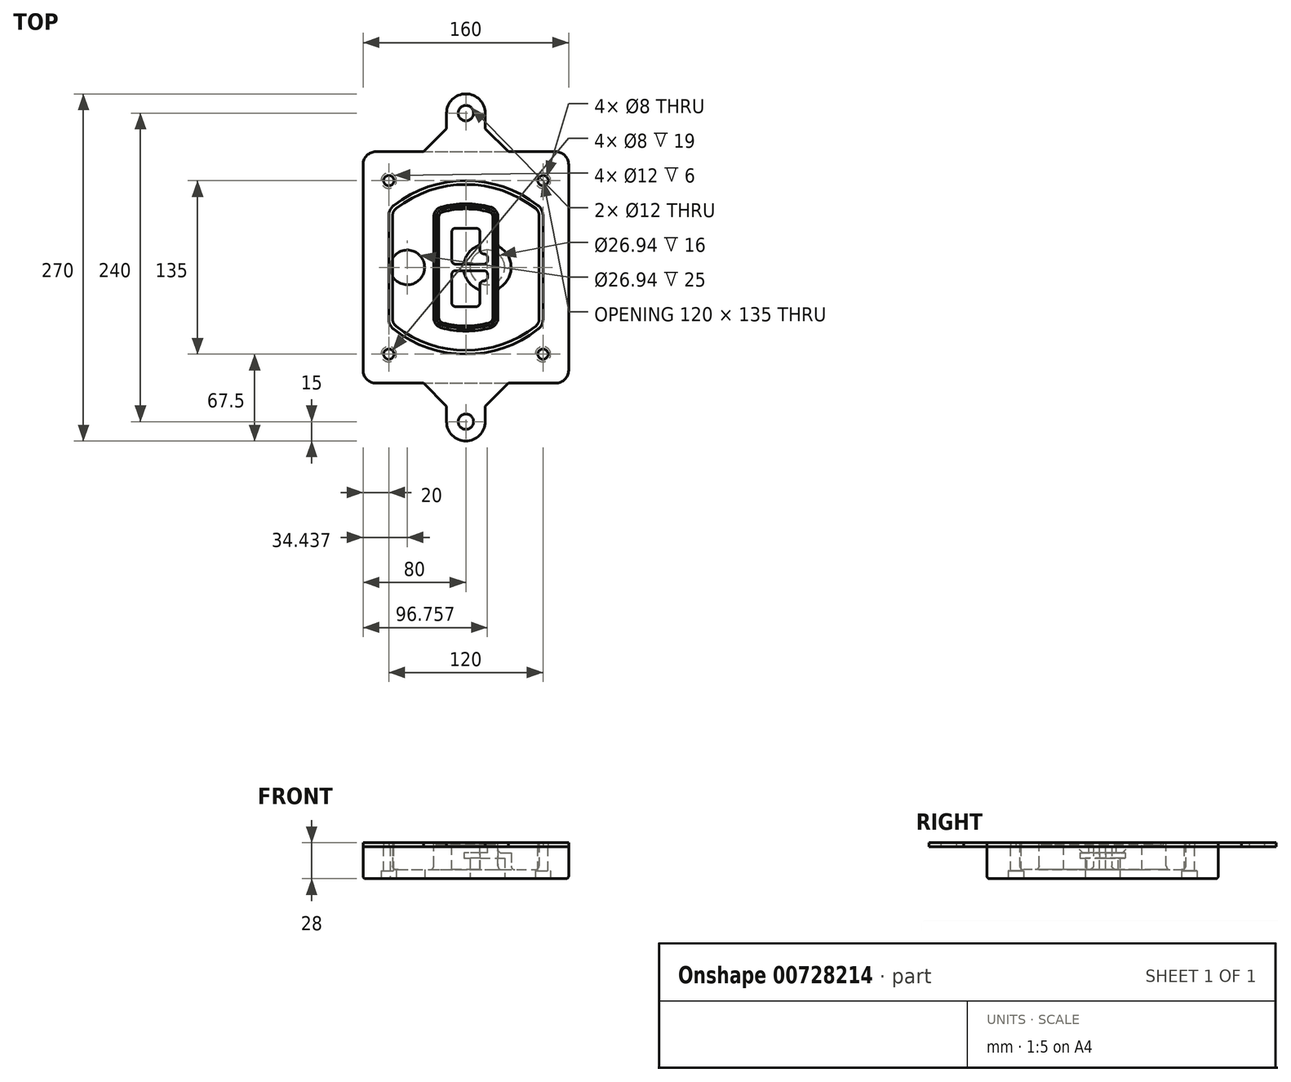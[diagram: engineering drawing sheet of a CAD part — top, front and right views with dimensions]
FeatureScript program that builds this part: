
annotation { "Feature Type Name" : "Feature", "Feature Type Description" : "" }
export const myFeature = defineFeature(function(context is Context, id is Id, definition is map)
    precondition{}
    {
        {
            var Q0;
            Q0=qCreatedBy(makeId("Top.planeOp"),FACE);
            var sketch = newSketch(context, id + "F0", { "sketchPlane" : qUnion([Q0])});
            skPoint(sketch, "E0.rect.middle", {"position": v(0, 0) * mm});
            skLineSegment(sketch, "E1.bottom", {"start": v(-70, -90) * mm, "end": v(70, -90) * mm});
            skLineSegment(sketch, "E1.top", {"start": v(-70, 90) * mm, "end": v(70, 90) * mm});
            skLineSegment(sketch, "E1.left", {"start": v(-80, -80) * mm, "end": v(-80, 80) * mm});
            skLineSegment(sketch, "E1.right", {"start": v(80, -80) * mm, "end": v(80, 80) * mm});
            skLineSegment(sketch, "E2", {"start": v(-80, 90) * mm, "end": v(80, -90) * mm, "construction": true});
            skLineSegment(sketch, "E3", {"start": v(80, 90) * mm, "end": v(-80, -90) * mm, "construction": true});
            skCircle(sketch, "E4", {"center": v(-60, 67.5) * mm, "radius": 4 * mm});
            skCircle(sketch, "E5", {"center": v(60, 67.5) * mm, "radius": 4 * mm});
            skCircle(sketch, "E6", {"center": v(60, -67.5) * mm, "radius": 4 * mm});
            skCircle(sketch, "E7", {"center": v(-60, -67.5) * mm, "radius": 4 * mm});
            skLineSegment(sketch, "E8", {"start": v(-60, 67.5) * mm, "end": v(60, 67.5) * mm, "construction": true});
            skLineSegment(sketch, "E9", {"start": v(60, 67.5) * mm, "end": v(60, -67.5) * mm, "construction": true});
            skLineSegment(sketch, "E10", {"start": v(60, -67.5) * mm, "end": v(-60, -67.5) * mm, "construction": true});
            skLineSegment(sketch, "E11", {"start": v(-60, -67.5) * mm, "end": v(-60, 67.5) * mm, "construction": true});
            skLineSegment(sketch, "E12", {"start": v(-60, 40.3) * mm, "end": v(-60, -40.3) * mm});
            skLineSegment(sketch, "E13", {"start": v(60, 40.3) * mm, "end": v(60, -40.3) * mm});
            skArc(sketch, "E14", {"start": v(56.15, 48.18) * mm, "mid": v(0, 67.5) * mm, "end": v(-56.15, 48.18) * mm});
            skArc(sketch, "E15", {"start": v(-56.15, -48.18) * mm, "mid": v(0, -67.5) * mm, "end": v(56.15, -48.18) * mm});
            skLineSegment(sketch, "E16", {"start": v(-60, 0) * mm, "end": v(60, 0) * mm, "construction": true});
            skPoint(sketch, "E17.visualSharp", {"position": v(-60, -45) * mm});
            skArc(sketch, "E17.filletArc", {"start": v(-60, -40.3) * mm, "mid": v(-58.99, -44.68) * mm, "end": v(-56.15, -48.18) * mm});
            skPoint(sketch, "E18.visualSharp", {"position": v(-60, 45) * mm});
            skArc(sketch, "E18.filletArc", {"start": v(-56.15, 48.18) * mm, "mid": v(-58.99, 44.68) * mm, "end": v(-60, 40.3) * mm});
            skPoint(sketch, "E19.visualSharp", {"position": v(60, 45) * mm});
            skArc(sketch, "E19.filletArc", {"start": v(60, 40.3) * mm, "mid": v(58.99, 44.68) * mm, "end": v(56.15, 48.18) * mm});
            skPoint(sketch, "E20.visualSharp", {"position": v(60, -45) * mm});
            skArc(sketch, "E20.filletArc", {"start": v(56.15, -48.18) * mm, "mid": v(58.99, -44.68) * mm, "end": v(60, -40.3) * mm});
            skPoint(sketch, "E21.visualSharp", {"position": v(-80, 90) * mm});
            skArc(sketch, "E21.filletArc", {"start": v(-70, 90) * mm, "mid": v(-77.07, 87.07) * mm, "end": v(-80, 80) * mm});
            skPoint(sketch, "E22.visualSharp", {"position": v(80, 90) * mm});
            skArc(sketch, "E22.filletArc", {"start": v(80, 80) * mm, "mid": v(77.07, 87.07) * mm, "end": v(70, 90) * mm});
            skPoint(sketch, "E23.visualSharp", {"position": v(80, -90) * mm});
            skArc(sketch, "E23.filletArc", {"start": v(70, -90) * mm, "mid": v(77.07, -87.07) * mm, "end": v(80, -80) * mm});
            skPoint(sketch, "E24.visualSharp", {"position": v(-80, -90) * mm});
            skArc(sketch, "E24.filletArc", {"start": v(-80, -80) * mm, "mid": v(-77.07, -87.07) * mm, "end": v(-70, -90) * mm});
            skArc(sketch, "E25.0", {"start": v(57, 40.3) * mm, "mid": v(56.3, 43.36) * mm, "end": v(54.3, 45.81) * mm});
            skLineSegment(sketch, "E25.1", {"start": v(57, 40.3) * mm, "end": v(57, -40.3) * mm});
            skArc(sketch, "E25.2", {"start": v(54.3, -45.81) * mm, "mid": v(56.3, -43.36) * mm, "end": v(57, -40.3) * mm});
            skArc(sketch, "E25.3", {"start": v(-54.3, -45.81) * mm, "mid": v(0, -64.5) * mm, "end": v(54.3, -45.81) * mm});
            skArc(sketch, "E25.4", {"start": v(-57, -40.3) * mm, "mid": v(-56.3, -43.36) * mm, "end": v(-54.3, -45.81) * mm});
            skArc(sketch, "E25.5", {"start": v(54.3, 45.81) * mm, "mid": v(0, 64.5) * mm, "end": v(-54.3, 45.81) * mm});
            skLineSegment(sketch, "E25.6", {"start": v(-57, 40.3) * mm, "end": v(-57, -40.3) * mm});
            skArc(sketch, "E25.7", {"start": v(-54.3, 45.81) * mm, "mid": v(-56.3, 43.36) * mm, "end": v(-57, 40.3) * mm});
            skArc(sketch, "E26.0", {"start": v(-58.62, 51.33) * mm, "mid": v(-62.58, 46.43) * mm, "end": v(-64, 40.3) * mm});
            skArc(sketch, "E26.1", {"start": v(58.62, 51.33) * mm, "mid": v(0, 71.5) * mm, "end": v(-58.62, 51.33) * mm});
            skArc(sketch, "E26.2", {"start": v(64, 40.3) * mm, "mid": v(62.58, 46.43) * mm, "end": v(58.62, 51.33) * mm});
            skLineSegment(sketch, "E26.3", {"start": v(64, 40.3) * mm, "end": v(64, -40.3) * mm});
            skArc(sketch, "E26.4", {"start": v(58.62, -51.33) * mm, "mid": v(62.58, -46.43) * mm, "end": v(64, -40.3) * mm});
            skLineSegment(sketch, "E26.5", {"start": v(-64, 40.3) * mm, "end": v(-64, -40.3) * mm});
            skArc(sketch, "E26.6", {"start": v(-58.62, -51.33) * mm, "mid": v(0, -71.5) * mm, "end": v(58.62, -51.33) * mm});
            skArc(sketch, "E26.7", {"start": v(-64, -40.3) * mm, "mid": v(-62.58, -46.43) * mm, "end": v(-58.62, -51.33) * mm});
            skSolve(sketch);
        }
        {
            var Q0;
            Q0=makeQuery(id+"F0.imprint","IMPRINT",FACE,{"disambiguationData":[TD([[makeQuery(id+"F0.imprint","IMPRINT",EDGE,{"derivedFrom":sQuery(id+"F0.wireOp",EDGE,"E1.bottom")}),1.0]])]});
            var Q1;
            Q1=makeQuery(id+"F0.imprint","IMPRINT",FACE,{"disambiguationData":[TD([[makeQuery(id+"F0.imprint","IMPRINT",EDGE,{"derivedFrom":sQuery(id+"F0.wireOp",EDGE,"E12")}),1.0]])]});
            var Q2;
            Q2=makeQuery(id+"F0.imprint","IMPRINT",FACE,{"disambiguationData":[TD([[makeQuery(id+"F0.imprint","IMPRINT",EDGE,{"derivedFrom":sQuery(id+"F0.wireOp",EDGE,"E25.0")}),1.0]])]});
            var Q3;
            Q3=makeQuery(id+"F0.imprint","IMPRINT",FACE,{"disambiguationData":[TD([[makeQuery(id+"F0.imprint","IMPRINT",EDGE,{"derivedFrom":sQuery(id+"F0.wireOp",EDGE,"E12")}),-1.0]])]});
            extrude(context, id + "F1", {"entities" : qUnion([Q0, Q1, Q2, Q3]), "oppositeDirection" : true, "depth" : 25 * mm, "offsetDistance" : 25 * mm});
        }
        {
            var Q0;
            Q0=makeQuery(id+"F0.imprint","IMPRINT",FACE,{"disambiguationData":[TD([[makeQuery(id+"F0.imprint","IMPRINT",EDGE,{"derivedFrom":sQuery(id+"F0.wireOp",EDGE,"E12")}),1.0]])]});
            extrude(context, id + "F2", {"entities" : qUnion([Q0]), "operationType" : NewBodyOperationType.ADD, "depth" : 3 * mm});
        }
        {
            var Q0;
            Q0=makeQuery(id+"F0.imprint","IMPRINT",FACE,{"disambiguationData":[TD([[makeQuery(id+"F0.imprint","IMPRINT",EDGE,{"derivedFrom":sQuery(id+"F0.wireOp",EDGE,"E25.0")}),1.0]])]});
            extrude(context, id + "F3", {"entities" : qUnion([Q0]), "operationType" : NewBodyOperationType.REMOVE, "oppositeDirection" : true, "depth" : 18 * mm});
        }
        {
            var Q0;
            Q0=makeQuery(id+"F2.opExtrude","CAP_FACE",FACE,{"disambiguationData":[OSD([sQuery(id+"F0.wireOp",EDGE,"E12"),sQuery(id+"F0.wireOp",EDGE,"E13"),sQuery(id+"F0.wireOp",EDGE,"E14"),sQuery(id+"F0.wireOp",EDGE,"E15"),sQuery(id+"F0.wireOp",EDGE,"E17.filletArc"),sQuery(id+"F0.wireOp",EDGE,"E18.filletArc"),sQuery(id+"F0.wireOp",EDGE,"E19.filletArc"),sQuery(id+"F0.wireOp",EDGE,"E20.filletArc"),sQuery(id+"F0.wireOp",EDGE,"E25.0"),sQuery(id+"F0.wireOp",EDGE,"E25.1"),sQuery(id+"F0.wireOp",EDGE,"E25.2"),sQuery(id+"F0.wireOp",EDGE,"E25.3"),sQuery(id+"F0.wireOp",EDGE,"E25.4"),sQuery(id+"F0.wireOp",EDGE,"E25.5"),sQuery(id+"F0.wireOp",EDGE,"E25.6"),sQuery(id+"F0.wireOp",EDGE,"E25.7")])],"isStart":false});
            var sketch = newSketch(context, id + "F4", { "sketchPlane" : qUnion([Q0])});
            skArc(sketch, "E27.0", {"start": v(-19.08, -46.97) * mm, "mid": v(0, -49.5) * mm, "end": v(19.08, -46.97) * mm});
            skArc(sketch, "E28.0", {"start": v(19.08, 46.97) * mm, "mid": v(0, 49.5) * mm, "end": v(-19.08, 46.97) * mm});
            skLineSegment(sketch, "E29", {"start": v(-25, 39.25) * mm, "end": v(-25, -39.25) * mm});
            skLineSegment(sketch, "E30", {"start": v(25, 39.25) * mm, "end": v(25, -39.25) * mm});
            skLineSegment(sketch, "E31", {"start": v(-25, 45.1) * mm, "end": v(25, 45.1) * mm, "construction": true});
            skLineSegment(sketch, "E32", {"start": v(-25, -45.1) * mm, "end": v(25, -45.1) * mm, "construction": true});
            skPoint(sketch, "E33.visualSharp", {"position": v(-25, 45.1) * mm});
            skArc(sketch, "E33.filletArc", {"start": v(-19.08, 46.97) * mm, "mid": v(-23.35, 44.11) * mm, "end": v(-25, 39.25) * mm});
            skPoint(sketch, "E34.visualSharp", {"position": v(25, 45.1) * mm});
            skArc(sketch, "E34.filletArc", {"start": v(25, 39.25) * mm, "mid": v(23.35, 44.11) * mm, "end": v(19.08, 46.97) * mm});
            skPoint(sketch, "E35.visualSharp", {"position": v(25, -45.1) * mm});
            skArc(sketch, "E35.filletArc", {"start": v(19.08, -46.97) * mm, "mid": v(23.35, -44.11) * mm, "end": v(25, -39.25) * mm});
            skPoint(sketch, "E36.visualSharp", {"position": v(-25, -45.1) * mm});
            skArc(sketch, "E36.filletArc", {"start": v(-25, -39.25) * mm, "mid": v(-23.35, -44.11) * mm, "end": v(-19.08, -46.97) * mm});
            skArc(sketch, "E37.0", {"start": v(54.3, 45.81) * mm, "mid": v(0, 64.5) * mm, "end": v(-54.3, 45.81) * mm});
            skArc(sketch, "E37.1", {"start": v(-54.3, 45.81) * mm, "mid": v(-56.3, 43.36) * mm, "end": v(-57, 40.3) * mm});
            skLineSegment(sketch, "E37.2", {"start": v(-57, 40.3) * mm, "end": v(-57, -40.3) * mm});
            skArc(sketch, "E37.3", {"start": v(-57, -40.3) * mm, "mid": v(-56.3, -43.36) * mm, "end": v(-54.3, -45.81) * mm});
            skArc(sketch, "E37.4", {"start": v(-54.3, -45.81) * mm, "mid": v(0, -64.5) * mm, "end": v(54.3, -45.81) * mm});
            skArc(sketch, "E37.5", {"start": v(54.3, -45.81) * mm, "mid": v(56.3, -43.36) * mm, "end": v(57, -40.3) * mm});
            skLineSegment(sketch, "E37.6", {"start": v(57, 40.3) * mm, "end": v(57, -40.3) * mm});
            skArc(sketch, "E37.7", {"start": v(57, 40.3) * mm, "mid": v(56.3, 43.36) * mm, "end": v(54.3, 45.81) * mm});
            skLineSegment(sketch, "E38.0", {"start": v(23, 39.25) * mm, "end": v(23, -39.25) * mm});
            skArc(sketch, "E38.1", {"start": v(18.56, -45.04) * mm, "mid": v(21.76, -42.9) * mm, "end": v(23, -39.25) * mm});
            skArc(sketch, "E38.2", {"start": v(-18.56, -45.04) * mm, "mid": v(0, -47.5) * mm, "end": v(18.56, -45.04) * mm});
            skArc(sketch, "E38.3", {"start": v(-23, -39.25) * mm, "mid": v(-21.76, -42.9) * mm, "end": v(-18.56, -45.04) * mm});
            skLineSegment(sketch, "E38.4", {"start": v(-23, 39.25) * mm, "end": v(-23, -39.25) * mm});
            skArc(sketch, "E38.5", {"start": v(23, 39.25) * mm, "mid": v(21.76, 42.9) * mm, "end": v(18.56, 45.04) * mm});
            skArc(sketch, "E38.6", {"start": v(-18.56, 45.04) * mm, "mid": v(-21.76, 42.9) * mm, "end": v(-23, 39.25) * mm});
            skArc(sketch, "E38.7", {"start": v(18.56, 45.04) * mm, "mid": v(0, 47.5) * mm, "end": v(-18.56, 45.04) * mm});
            skArc(sketch, "E39.0", {"start": v(21, 39.25) * mm, "mid": v(20.18, 41.68) * mm, "end": v(18.04, 43.1) * mm});
            skLineSegment(sketch, "E39.1", {"start": v(21, 39.25) * mm, "end": v(21, -39.25) * mm});
            skArc(sketch, "E39.2", {"start": v(18.04, -43.1) * mm, "mid": v(20.18, -41.68) * mm, "end": v(21, -39.25) * mm});
            skArc(sketch, "E39.3", {"start": v(-18.04, -43.1) * mm, "mid": v(0, -45.5) * mm, "end": v(18.04, -43.1) * mm});
            skArc(sketch, "E39.4", {"start": v(-21, -39.25) * mm, "mid": v(-20.18, -41.68) * mm, "end": v(-18.04, -43.1) * mm});
            skArc(sketch, "E39.5", {"start": v(18.04, 43.1) * mm, "mid": v(0, 45.5) * mm, "end": v(-18.04, 43.1) * mm});
            skLineSegment(sketch, "E39.6", {"start": v(-21, 39.25) * mm, "end": v(-21, -39.25) * mm});
            skArc(sketch, "E39.7", {"start": v(-18.04, 43.1) * mm, "mid": v(-20.18, 41.68) * mm, "end": v(-21, 39.25) * mm});
            skLineSegment(sketch, "E40", {"start": v(-25, 0) * mm, "end": v(25, 0) * mm, "construction": true});
            skLineSegment(sketch, "E41", {"start": v(-11, 5.5) * mm, "end": v(-11, 27.5) * mm});
            skLineSegment(sketch, "E42", {"start": v(-8, 30.5) * mm, "end": v(8, 30.5) * mm});
            skLineSegment(sketch, "E43", {"start": v(11, 27.5) * mm, "end": v(11, 13.5) * mm});
            skLineSegment(sketch, "E44", {"start": v(14, 10.5) * mm, "end": v(14, 10.5) * mm});
            skLineSegment(sketch, "E45", {"start": v(17, 7.5) * mm, "end": v(17, 5.5) * mm});
            skLineSegment(sketch, "E46", {"start": v(14, 2.5) * mm, "end": v(-8, 2.5) * mm});
            skPoint(sketch, "E47.visualSharp", {"position": v(-11, 30.5) * mm});
            skArc(sketch, "E47.filletArc", {"start": v(-8, 30.5) * mm, "mid": v(-10.12, 29.62) * mm, "end": v(-11, 27.5) * mm});
            skPoint(sketch, "E48.visualSharp", {"position": v(11, 30.5) * mm});
            skArc(sketch, "E48.filletArc", {"start": v(11, 27.5) * mm, "mid": v(10.12, 29.62) * mm, "end": v(8, 30.5) * mm});
            skPoint(sketch, "E49.visualSharp", {"position": v(11, 10.5) * mm});
            skArc(sketch, "E49.filletArc", {"start": v(11, 13.5) * mm, "mid": v(11.88, 11.38) * mm, "end": v(14, 10.5) * mm});
            skPoint(sketch, "E50.visualSharp", {"position": v(17, 10.5) * mm});
            skArc(sketch, "E50.filletArc", {"start": v(17, 7.5) * mm, "mid": v(16.12, 9.62) * mm, "end": v(14, 10.5) * mm});
            skPoint(sketch, "E51.visualSharp", {"position": v(17, 2.5) * mm});
            skArc(sketch, "E51.filletArc", {"start": v(14, 2.5) * mm, "mid": v(16.12, 3.38) * mm, "end": v(17, 5.5) * mm});
            skPoint(sketch, "E52.visualSharp", {"position": v(-11, 2.5) * mm});
            skArc(sketch, "E52.filletArc", {"start": v(-11, 5.5) * mm, "mid": v(-10.12, 3.38) * mm, "end": v(-8, 2.5) * mm});
            skLineSegment(sketch, "E53.0.MirrorCS", {"start": v(14, -2.5) * mm, "end": v(-8, -2.5) * mm});
            skArc(sketch, "E54.0.MirrorCS", {"start": v(-11, -5.5) * mm, "mid": v(-10.12, -3.38) * mm, "end": v(-8, -2.5) * mm});
            skLineSegment(sketch, "E55.0.MirrorCS", {"start": v(-11, -5.5) * mm, "end": v(-11, -27.5) * mm});
            skArc(sketch, "E56.0.MirrorCS", {"start": v(-8, -30.5) * mm, "mid": v(-10.12, -29.62) * mm, "end": v(-11, -27.5) * mm});
            skLineSegment(sketch, "E57.0.MirrorCS", {"start": v(-8, -30.5) * mm, "end": v(8, -30.5) * mm});
            skArc(sketch, "E58.0.MirrorCS", {"start": v(11, -27.5) * mm, "mid": v(10.12, -29.62) * mm, "end": v(8, -30.5) * mm});
            skLineSegment(sketch, "E59.0.MirrorCS", {"start": v(11, -27.5) * mm, "end": v(11, -13.5) * mm});
            skArc(sketch, "E60.0.MirrorCS", {"start": v(11, -13.5) * mm, "mid": v(11.88, -11.38) * mm, "end": v(14, -10.5) * mm});
            skArc(sketch, "E61.0.MirrorCS", {"start": v(17, -7.5) * mm, "mid": v(16.12, -9.62) * mm, "end": v(14, -10.5) * mm});
            skLineSegment(sketch, "E62.0.MirrorCS", {"start": v(17, -7.5) * mm, "end": v(17, -5.5) * mm});
            skArc(sketch, "E63.0.MirrorCS", {"start": v(14, -2.5) * mm, "mid": v(16.12, -3.38) * mm, "end": v(17, -5.5) * mm});
            skSolve(sketch);
        }
        {
            var Q0;
            Q0=makeQuery(id+"F4.imprint","IMPRINT",FACE,{"disambiguationData":[TD([[makeQuery(id+"F4.imprint","IMPRINT",EDGE,{"derivedFrom":sQuery(id+"F4.wireOp",EDGE,"E27.0")}),1.0]])]});
            var Q1;
            Q1=makeQuery(id+"F4.imprint","IMPRINT",FACE,{"disambiguationData":[TD([[makeQuery(id+"F4.imprint","IMPRINT",EDGE,{"derivedFrom":sQuery(id+"F4.wireOp",EDGE,"E38.0")}),-1.0]])]});
            var Q2;
            Q2=makeQuery(id+"F4.imprint","IMPRINT",FACE,{"disambiguationData":[TD([[makeQuery(id+"F4.imprint","IMPRINT",EDGE,{"derivedFrom":sQuery(id+"F4.wireOp",EDGE,"E39.0")}),1.0]])]});
            extrude(context, id + "F5", {"entities" : qUnion([Q0, Q1, Q2]), "operationType" : NewBodyOperationType.ADD, "endBound" : BoundingType.UP_TO_NEXT, "oppositeDirection" : true, "depth" : 25 * mm});
        }
        {
            var Q0;
            Q0=makeQuery(id+"F4.imprint","IMPRINT",FACE,{"disambiguationData":[TD([[makeQuery(id+"F4.imprint","IMPRINT",EDGE,{"derivedFrom":sQuery(id+"F4.wireOp",EDGE,"E38.0")}),-1.0]])]});
            extrude(context, id + "F6", {"entities" : qUnion([Q0]), "operationType" : NewBodyOperationType.REMOVE, "oppositeDirection" : true, "depth" : 2 * mm});
        }
        {
            var Q0;
            Q0=makeQuery(id+"F1.opExtrude","CAP_FACE",FACE,{"disambiguationData":[OSD([sQuery(id+"F0.wireOp",EDGE,"E1.bottom"),sQuery(id+"F0.wireOp",EDGE,"E1.top"),sQuery(id+"F0.wireOp",EDGE,"E1.left"),sQuery(id+"F0.wireOp",EDGE,"E1.right"),sQuery(id+"F0.wireOp",EDGE,"E4"),sQuery(id+"F0.wireOp",EDGE,"E5"),sQuery(id+"F0.wireOp",EDGE,"E6"),sQuery(id+"F0.wireOp",EDGE,"E7"),sQuery(id+"F0.wireOp",EDGE,"E21.filletArc"),sQuery(id+"F0.wireOp",EDGE,"E22.filletArc"),sQuery(id+"F0.wireOp",EDGE,"E23.filletArc"),sQuery(id+"F0.wireOp",EDGE,"E24.filletArc")])],"isStart":false});
            var sketch = newSketch(context, id + "F7", { "sketchPlane" : qUnion([Q0])});
            skCircle(sketch, "E64", {"center": v(16.76, 0) * mm, "radius": 13.47 * mm});
            skCircle(sketch, "E65", {"center": v(-45.56, 0) * mm, "radius": 13.47 * mm});
            skLineSegment(sketch, "E66", {"start": v(80, 0) * mm, "end": v(-80, 0) * mm});
            skCircle(sketch, "E67", {"center": v(16.76, 0) * mm, "radius": 18.47 * mm});
            skCircle(sketch, "E68", {"center": v(60, -67.5) * mm, "radius": 6 * mm});
            skCircle(sketch, "E69", {"center": v(-60, -67.5) * mm, "radius": 6 * mm});
            skCircle(sketch, "E70", {"center": v(-60, 67.5) * mm, "radius": 6 * mm});
            skCircle(sketch, "E71", {"center": v(60, 67.5) * mm, "radius": 6 * mm});
            skSolve(sketch);
        }
        {
            var Q0;
            {var subQ1=sQuery(id+"F7.wireOp",EDGE,"E66");var subQ4=sQuery(id+"F7.wireOp",EDGE,"E64");var subQ6=makeQuery(id+"F7.imprint","INTERSECT",VERTEX,{"disambiguationData":[OD(0.0)],"derivedFrom":[subQ4,subQ1]});Q0=makeQuery(id+"F7.imprint","IMPRINT",FACE,{"disambiguationData":[TD([[makeQuery(id+"F7.imprint","IMPRINT",EDGE,{"disambiguationData":[TD([[subQ6,-1.0]])],"derivedFrom":subQ4}),-1.0]])]});}
            var Q1;
            {var subQ0=sQuery(id+"F7.wireOp",EDGE,"E66");var subQ1=sQuery(id+"F7.wireOp",EDGE,"E64");var subQ3=makeQuery(id+"F7.imprint","INTERSECT",VERTEX,{"disambiguationData":[OD(0.0)],"derivedFrom":[subQ1,subQ0]});Q1=makeQuery(id+"F7.imprint","IMPRINT",FACE,{"disambiguationData":[TD([[makeQuery(id+"F7.imprint","IMPRINT",EDGE,{"disambiguationData":[TD([[subQ3,-1.0]])],"derivedFrom":subQ1}),1.0]])]});}
            var Q2;
            {var subQ0=sQuery(id+"F7.wireOp",EDGE,"E66");var subQ1=sQuery(id+"F7.wireOp",EDGE,"E64");var subQ3=makeQuery(id+"F7.imprint","INTERSECT",VERTEX,{"disambiguationData":[OD(0.0)],"derivedFrom":[subQ1,subQ0]});Q2=makeQuery(id+"F7.imprint","IMPRINT",FACE,{"disambiguationData":[TD([[makeQuery(id+"F7.imprint","IMPRINT",EDGE,{"disambiguationData":[TD([[subQ3,1.0]])],"derivedFrom":subQ1}),1.0]])]});}
            var Q3;
            {var subQ1=sQuery(id+"F7.wireOp",EDGE,"E66");var subQ4=sQuery(id+"F7.wireOp",EDGE,"E64");var subQ6=makeQuery(id+"F7.imprint","INTERSECT",VERTEX,{"disambiguationData":[OD(0.0)],"derivedFrom":[subQ4,subQ1]});Q3=makeQuery(id+"F7.imprint","IMPRINT",FACE,{"disambiguationData":[TD([[makeQuery(id+"F7.imprint","IMPRINT",EDGE,{"disambiguationData":[TD([[subQ6,1.0]])],"derivedFrom":subQ4}),-1.0]])]});}
            extrude(context, id + "F8", {"entities" : qUnion([Q0, Q1, Q2, Q3]), "operationType" : NewBodyOperationType.ADD, "oppositeDirection" : true, "depth" : 20 * mm});
        }
        {
            var Q0;
            {var subQ0=sQuery(id+"F7.wireOp",EDGE,"E66");var subQ1=sQuery(id+"F7.wireOp",EDGE,"E64");var subQ3=makeQuery(id+"F7.imprint","INTERSECT",VERTEX,{"disambiguationData":[OD(0.0)],"derivedFrom":[subQ1,subQ0]});Q0=makeQuery(id+"F7.imprint","IMPRINT",FACE,{"disambiguationData":[TD([[makeQuery(id+"F7.imprint","IMPRINT",EDGE,{"disambiguationData":[TD([[subQ3,-1.0]])],"derivedFrom":subQ1}),1.0]])]});}
            var Q1;
            {var subQ0=sQuery(id+"F7.wireOp",EDGE,"E66");var subQ1=sQuery(id+"F7.wireOp",EDGE,"E64");var subQ3=makeQuery(id+"F7.imprint","INTERSECT",VERTEX,{"disambiguationData":[OD(0.0)],"derivedFrom":[subQ1,subQ0]});Q1=makeQuery(id+"F7.imprint","IMPRINT",FACE,{"disambiguationData":[TD([[makeQuery(id+"F7.imprint","IMPRINT",EDGE,{"disambiguationData":[TD([[subQ3,1.0]])],"derivedFrom":subQ1}),1.0]])]});}
            extrude(context, id + "F9", {"entities" : qUnion([Q0, Q1]), "operationType" : NewBodyOperationType.REMOVE, "oppositeDirection" : true, "depth" : 16 * mm});
        }
        {
            var Q0;
            {var subQ0=sQuery(id+"F7.wireOp",EDGE,"E66");var subQ1=sQuery(id+"F7.wireOp",EDGE,"E65");var subQ3=makeQuery(id+"F7.imprint","INTERSECT",VERTEX,{"disambiguationData":[OD(0.0)],"derivedFrom":[subQ1,subQ0]});Q0=makeQuery(id+"F7.imprint","IMPRINT",FACE,{"disambiguationData":[TD([[makeQuery(id+"F7.imprint","IMPRINT",EDGE,{"disambiguationData":[TD([[subQ3,-1.0]])],"derivedFrom":subQ1}),1.0]])]});}
            var Q1;
            {var subQ0=sQuery(id+"F7.wireOp",EDGE,"E66");var subQ1=sQuery(id+"F7.wireOp",EDGE,"E65");var subQ3=makeQuery(id+"F7.imprint","INTERSECT",VERTEX,{"disambiguationData":[OD(0.0)],"derivedFrom":[subQ1,subQ0]});Q1=makeQuery(id+"F7.imprint","IMPRINT",FACE,{"disambiguationData":[TD([[makeQuery(id+"F7.imprint","IMPRINT",EDGE,{"disambiguationData":[TD([[subQ3,1.0]])],"derivedFrom":subQ1}),1.0]])]});}
            extrude(context, id + "F10", {"entities" : qUnion([Q0, Q1]), "operationType" : NewBodyOperationType.REMOVE, "oppositeDirection" : true, "depth" : 25 * mm});
        }
        {
            var Q0;
            Q0=makeQuery(id+"F7.imprint","IMPRINT",FACE,{"disambiguationData":[TD([[makeQuery(id+"F7.imprint","IMPRINT",EDGE,{"derivedFrom":sQuery(id+"F7.wireOp",EDGE,"E68")}),1.0]])]});
            var Q1;
            Q1=makeQuery(id+"F7.imprint","IMPRINT",FACE,{"disambiguationData":[TD([[makeQuery(id+"F7.imprint","IMPRINT",EDGE,{"derivedFrom":makeQuery(id+"F1.opExtrude","CAP_EDGE",EDGE,{"disambiguationData":[OSD([sQuery(id+"F0.wireOp",EDGE,"E5")])],"isStart":false})}),-1.0]])]});
            var Q2;
            Q2=makeQuery(id+"F7.imprint","IMPRINT",FACE,{"disambiguationData":[TD([[makeQuery(id+"F7.imprint","IMPRINT",EDGE,{"derivedFrom":sQuery(id+"F7.wireOp",EDGE,"E69")}),1.0]])]});
            var Q3;
            Q3=makeQuery(id+"F7.imprint","IMPRINT",FACE,{"disambiguationData":[TD([[makeQuery(id+"F7.imprint","IMPRINT",EDGE,{"derivedFrom":makeQuery(id+"F1.opExtrude","CAP_EDGE",EDGE,{"disambiguationData":[OSD([sQuery(id+"F0.wireOp",EDGE,"E4")])],"isStart":false})}),-1.0]])]});
            var Q4;
            Q4=makeQuery(id+"F7.imprint","IMPRINT",FACE,{"disambiguationData":[TD([[makeQuery(id+"F7.imprint","IMPRINT",EDGE,{"derivedFrom":sQuery(id+"F7.wireOp",EDGE,"E70")}),1.0]])]});
            var Q5;
            Q5=makeQuery(id+"F7.imprint","IMPRINT",FACE,{"disambiguationData":[TD([[makeQuery(id+"F7.imprint","IMPRINT",EDGE,{"derivedFrom":makeQuery(id+"F1.opExtrude","CAP_EDGE",EDGE,{"disambiguationData":[OSD([sQuery(id+"F0.wireOp",EDGE,"E7")])],"isStart":false})}),-1.0]])]});
            var Q6;
            Q6=makeQuery(id+"F7.imprint","IMPRINT",FACE,{"disambiguationData":[TD([[makeQuery(id+"F7.imprint","IMPRINT",EDGE,{"derivedFrom":sQuery(id+"F7.wireOp",EDGE,"E71")}),1.0]])]});
            var Q7;
            Q7=makeQuery(id+"F7.imprint","IMPRINT",FACE,{"disambiguationData":[TD([[makeQuery(id+"F7.imprint","IMPRINT",EDGE,{"derivedFrom":makeQuery(id+"F1.opExtrude","CAP_EDGE",EDGE,{"disambiguationData":[OSD([sQuery(id+"F0.wireOp",EDGE,"E6")])],"isStart":false})}),-1.0]])]});
            extrude(context, id + "F11", {"entities" : qUnion([Q0, Q1, Q2, Q3, Q4, Q5, Q6, Q7]), "operationType" : NewBodyOperationType.REMOVE, "oppositeDirection" : true, "depth" : 6 * mm});
        }
        {
            var Q0;
            Q0=makeQuery(id+"F9.boolean.opBoolean","COPY",FACE,{"derivedFrom":makeQuery(id+"F9.opExtrude","CAP_FACE",FACE,{"disambiguationData":[OSD([sQuery(id+"F7.wireOp",EDGE,"E64")])],"isStart":false})});
            var sketch = newSketch(context, id + "F12", { "sketchPlane" : qUnion([Q0])});
            skArc(sketch, "E72.0", {"start": v(11, 17.55) * mm, "mid": v(2.57, 11.82) * mm, "end": v(-1.54, 2.5) * mm});
            skArc(sketch, "E72.1", {"start": v(-1.54, -2.5) * mm, "mid": v(2.57, -11.82) * mm, "end": v(11, -17.55) * mm});
            skLineSegment(sketch, "E73", {"start": v(-1.54, -2.5) * mm, "end": v(14, -2.5) * mm});
            skLineSegment(sketch, "E74.0", {"start": v(14, 2.5) * mm, "end": v(-1.54, 2.5) * mm});
            skArc(sketch, "E74.1", {"start": v(14, 2.5) * mm, "mid": v(16.12, 3.38) * mm, "end": v(17, 5.5) * mm});
            skLineSegment(sketch, "E74.2", {"start": v(17, 7.5) * mm, "end": v(17, 5.5) * mm});
            skArc(sketch, "E74.3", {"start": v(17, 7.5) * mm, "mid": v(16.12, 9.62) * mm, "end": v(14, 10.5) * mm});
            skArc(sketch, "E74.4", {"start": v(11, 13.5) * mm, "mid": v(11.88, 11.38) * mm, "end": v(14, 10.5) * mm});
            skLineSegment(sketch, "E74.5", {"start": v(11, 17.55) * mm, "end": v(11, 13.5) * mm});
            skLineSegment(sketch, "E74.7", {"start": v(14, -2.5) * mm, "end": v(-1.54, -2.5) * mm});
            skArc(sketch, "E74.8", {"start": v(14, -2.5) * mm, "mid": v(16.12, -3.38) * mm, "end": v(17, -5.5) * mm});
            skLineSegment(sketch, "E74.9", {"start": v(17, -7.5) * mm, "end": v(17, -5.5) * mm});
            skArc(sketch, "E74.10", {"start": v(17, -7.5) * mm, "mid": v(16.12, -9.62) * mm, "end": v(14, -10.5) * mm});
            skArc(sketch, "E74.11", {"start": v(11, -13.5) * mm, "mid": v(11.88, -11.38) * mm, "end": v(14, -10.5) * mm});
            skLineSegment(sketch, "E74.12", {"start": v(11, -17.55) * mm, "end": v(11, -13.5) * mm});
            skPoint(sketch, "E75.orphan", {"position": v(11, -27.5) * mm});
            skPoint(sketch, "E76.orphan", {"position": v(-8, -2.5) * mm});
            skPoint(sketch, "E77.orphan", {"position": v(-8, 2.5) * mm});
            skPoint(sketch, "E78.orphan", {"position": v(11, 27.5) * mm});
            skSolve(sketch);
        }
        {
            var Q0;
            {var subQ7=sQuery(id+"F12.wireOp",EDGE,"E72.0");var subQ14=sQuery(id+"F12.wireOp",EDGE,"E72.1");var subQ16=sQuery(id+"F12.wireOp",EDGE,"E74.1");var subQ18=sQuery(id+"F12.wireOp",EDGE,"E74.8");Q0=qUnion([makeQuery(id+"F12.imprint","IMPRINT",FACE,{"disambiguationData":[TD([[makeQuery(id+"F12.imprint","IMPRINT",EDGE,{"derivedFrom":subQ7}),1.0]])]}),makeQuery(id+"F12.imprint","IMPRINT",FACE,{"disambiguationData":[TD([[makeQuery(id+"F12.imprint","IMPRINT",EDGE,{"derivedFrom":subQ14}),1.0]])]}),makeQuery(id+"F12.imprint","IMPRINT",FACE,{"disambiguationData":[TD([[makeQuery(id+"F12.imprint","IMPRINT",EDGE,{"derivedFrom":subQ16}),1.0]])]}),makeQuery(id+"F12.imprint","IMPRINT",FACE,{"disambiguationData":[TD([[makeQuery(id+"F12.imprint","IMPRINT",EDGE,{"derivedFrom":subQ18}),-1.0]])]})]);}
            var Q1;
            Q1=makeQuery(id+"F5.boolean.opBoolean","SPLIT",FACE,{"disambiguationData":[TD([makeQuery(id+"F5.opExtrude","SWEPT_FACE",FACE,{"disambiguationData":[OSD([sQuery(id+"F4.wireOp",EDGE,"E41")])]})])],"derivedFrom":makeQuery(id+"F3.boolean.opBoolean","COPY",FACE,{"derivedFrom":makeQuery(id+"F3.opExtrude","CAP_FACE",FACE,{"disambiguationData":[OSD([sQuery(id+"F0.wireOp",EDGE,"E25.0"),sQuery(id+"F0.wireOp",EDGE,"E25.1"),sQuery(id+"F0.wireOp",EDGE,"E25.2"),sQuery(id+"F0.wireOp",EDGE,"E25.3"),sQuery(id+"F0.wireOp",EDGE,"E25.4"),sQuery(id+"F0.wireOp",EDGE,"E25.5"),sQuery(id+"F0.wireOp",EDGE,"E25.6"),sQuery(id+"F0.wireOp",EDGE,"E25.7")])],"isStart":false})})});
            extrude(context, id + "F13", {"entities" : qUnion([Q0]), "operationType" : NewBodyOperationType.REMOVE, "endBound" : BoundingType.UP_TO_SURFACE, "endBoundEntityFace" : qUnion([Q1]), "depth" : 25 * mm});
        }
        {
            var Q0;
            Q0=makeQuery(id+"F3.boolean.opBoolean","COPY",EDGE,{"derivedFrom":makeQuery(id+"F3.opExtrude","CAP_EDGE",EDGE,{"disambiguationData":[OSD([sQuery(id+"F0.wireOp",EDGE,"E25.6")])],"isStart":false})});
            var Q1;
            Q1=makeQuery(id+"F8.boolean.opBoolean","INTERSECT",EDGE,{"derivedFrom":[makeQuery(id+"F5.opExtrude","SWEPT_FACE",FACE,{"disambiguationData":[OSD([sQuery(id+"F4.wireOp",EDGE,"E30")])]}),makeQuery(id+"F8.opExtrude","CAP_FACE",FACE,{"disambiguationData":[OSD([sQuery(id+"F7.wireOp",EDGE,"E67")])],"isStart":false})]});
            var Q2;
            Q2=makeQuery(id+"F8.boolean.opBoolean","INTERSECT",EDGE,{"disambiguationData":[OD(1.0)],"derivedFrom":[makeQuery(id+"F5.opExtrude","SWEPT_FACE",FACE,{"disambiguationData":[OSD([sQuery(id+"F4.wireOp",EDGE,"E30")])]}),makeQuery(id+"F8.opExtrude","SWEPT_FACE",FACE,{"disambiguationData":[OSD([sQuery(id+"F7.wireOp",EDGE,"E67")])]})]});
            var Q3;
            {var subQ0=sQuery(id+"F4.wireOp",EDGE,"E30");Q3=makeQuery(id+"F8.boolean.opBoolean","SPLIT",EDGE,{"disambiguationData":[TD([makeQuery(id+"F5.opExtrude","SWEPT_FACE",FACE,{"disambiguationData":[OSD([sQuery(id+"F4.wireOp",EDGE,"E35.filletArc")])]})])],"derivedFrom":makeQuery(id+"F5.opExtrude","CAP_EDGE",EDGE,{"disambiguationData":[OSD([subQ0])],"isStart":false})});}
            var Q4;
            {var subQ0=sQuery(id+"F0.wireOp",EDGE,"E25.7");var subQ1=sQuery(id+"F0.wireOp",EDGE,"E25.1");var subQ2=sQuery(id+"F0.wireOp",EDGE,"E25.6");var subQ3=sQuery(id+"F0.wireOp",EDGE,"E25.5");var subQ4=sQuery(id+"F0.wireOp",EDGE,"E25.4");var subQ5=sQuery(id+"F0.wireOp",EDGE,"E25.0");var subQ6=sQuery(id+"F0.wireOp",EDGE,"E25.2");var subQ7=sQuery(id+"F0.wireOp",EDGE,"E25.3");Q4=makeQuery(id+"F8.boolean.opBoolean","INTERSECT",EDGE,{"derivedFrom":[makeQuery(id+"F5.boolean.opBoolean","SPLIT",FACE,{"disambiguationData":[TD([makeQuery(id+"F2.opExtrude","SWEPT_FACE",FACE,{"disambiguationData":[OSD([subQ5])]})])],"derivedFrom":makeQuery(id+"F3.boolean.opBoolean","COPY",FACE,{"derivedFrom":makeQuery(id+"F3.opExtrude","CAP_FACE",FACE,{"disambiguationData":[OSD([subQ5,subQ1,subQ6,subQ7,subQ4,subQ3,subQ2,subQ0])],"isStart":false})})}),makeQuery(id+"F8.opExtrude","SWEPT_FACE",FACE,{"disambiguationData":[OSD([sQuery(id+"F7.wireOp",EDGE,"E67")])]})]});}
            var Q5;
            Q5=makeQuery(id+"F8.boolean.opBoolean","INTERSECT",EDGE,{"disambiguationData":[OD(0.0)],"derivedFrom":[makeQuery(id+"F5.opExtrude","SWEPT_FACE",FACE,{"disambiguationData":[OSD([sQuery(id+"F4.wireOp",EDGE,"E30")])]}),makeQuery(id+"F8.opExtrude","SWEPT_FACE",FACE,{"disambiguationData":[OSD([sQuery(id+"F7.wireOp",EDGE,"E67")])]})]});
            fillet(context, id + "F14", {"entities" : qUnion([Q0, Q1, Q2, Q3, Q4, Q5]), "radius" : 3 * mm, "tangentPropagation" : true, "allowEdgeOverflow" : false});
        }
        {
            var Q0;
            Q0=makeQuery(id+"F1.opExtrude","CAP_EDGE",EDGE,{"disambiguationData":[OSD([sQuery(id+"F0.wireOp",EDGE,"E1.bottom")])],"isStart":false});
            fillet(context, id + "F15", {"entities" : qUnion([Q0]), "radius" : 2 * mm, "tangentPropagation" : true, "allowEdgeOverflow" : false});
        }
        {
            var Q0;
            {var subQ0=sQuery(id+"F0.wireOp",EDGE,"E21.filletArc");var subQ1=sQuery(id+"F0.wireOp",EDGE,"E7");var subQ2=sQuery(id+"F0.wireOp",EDGE,"E6");var subQ3=sQuery(id+"F0.wireOp",EDGE,"E5");var subQ4=sQuery(id+"F0.wireOp",EDGE,"E4");var subQ5=sQuery(id+"F0.wireOp",EDGE,"E22.filletArc");var subQ6=sQuery(id+"F0.wireOp",EDGE,"E1.bottom");var subQ7=sQuery(id+"F0.wireOp",EDGE,"E1.right");var subQ8=sQuery(id+"F0.wireOp",EDGE,"E1.top");var subQ9=sQuery(id+"F0.wireOp",EDGE,"E1.left");var subQ10=sQuery(id+"F0.wireOp",EDGE,"E23.filletArc");var subQ11=sQuery(id+"F0.wireOp",EDGE,"E24.filletArc");Q0=makeQuery(id+"F2.boolean.opBoolean","SPLIT",FACE,{"disambiguationData":[TD([makeQuery(id+"F1.opExtrude","SWEPT_FACE",FACE,{"disambiguationData":[OSD([subQ6])]})])],"derivedFrom":makeQuery(id+"F1.opExtrude","CAP_FACE",FACE,{"disambiguationData":[OSD([subQ6,subQ8,subQ9,subQ7,subQ4,subQ3,subQ2,subQ1,subQ0,subQ5,subQ10,subQ11])],"isStart":true})});}
            var sketch = newSketch(context, id + "F16", { "sketchPlane" : qUnion([Q0])});
            skLineSegment(sketch, "E79", {"start": v(-33, 90) * mm, "end": v(-15, 108) * mm});
            skLineSegment(sketch, "E80", {"start": v(33, 90) * mm, "end": v(15, 108) * mm});
            skLineSegment(sketch, "E81", {"start": v(15, 108) * mm, "end": v(15, 120) * mm});
            skLineSegment(sketch, "E82", {"start": v(-15, 108) * mm, "end": v(-15, 120) * mm});
            skArc(sketch, "E83", {"start": v(15, 120) * mm, "mid": v(0, 135) * mm, "end": v(-15, 120) * mm});
            skCircle(sketch, "E84", {"center": v(0, 120) * mm, "radius": 6 * mm});
            skLineSegment(sketch, "E85", {"start": v(0, 120) * mm, "end": v(0, 90) * mm, "construction": true});
            skLineSegment(sketch, "E86", {"start": v(80, 0) * mm, "end": v(-80, 0) * mm, "construction": true});
            skLineSegment(sketch, "E87.MirrorCS", {"start": v(-33, -90) * mm, "end": v(-15, -108) * mm});
            skCircle(sketch, "E88.MirrorC", {"center": v(0, -120) * mm, "radius": 6 * mm});
            skLineSegment(sketch, "E89.MirrorCS", {"start": v(-15, -108) * mm, "end": v(-15, -120) * mm});
            skLineSegment(sketch, "E90.MirrorCS", {"start": v(33, -90) * mm, "end": v(15, -108) * mm});
            skLineSegment(sketch, "E91.MirrorCS", {"start": v(15, -108) * mm, "end": v(15, -120) * mm});
            skArc(sketch, "E92.MirrorCS", {"start": v(15, -120) * mm, "mid": v(0, -135) * mm, "end": v(-15, -120) * mm});
            skSolve(sketch);
        }
        {
            var Q0;
            {var subQ0=sQuery(id+"F16.wireOp",EDGE,"E79");Q0=makeQuery(id+"F16.imprint","IMPRINT",FACE,{"disambiguationData":[TD([[makeQuery(id+"F16.imprint","IMPRINT",EDGE,{"derivedFrom":subQ0}),-1.0]])]});}
            var Q1;
            Q1=makeQuery(id+"F16.imprint","IMPRINT",FACE,{"disambiguationData":[TD([[makeQuery(id+"F16.imprint","IMPRINT",EDGE,{"derivedFrom":makeQuery(id+"F1.opExtrude","CAP_EDGE",EDGE,{"disambiguationData":[OSD([sQuery(id+"F0.wireOp",EDGE,"E1.left")])],"isStart":true})}),-1.0]])]});
            var Q2;
            {var subQ1=sQuery(id+"F16.wireOp",EDGE,"E87.MirrorCS");Q2=makeQuery(id+"F16.imprint","IMPRINT",FACE,{"disambiguationData":[TD([[makeQuery(id+"F16.imprint","IMPRINT",EDGE,{"derivedFrom":subQ1}),1.0]])]});}
            var Q3;
            Q3=makeQuery(id+"F2.opExtrude","CAP_FACE",FACE,{"disambiguationData":[OSD([sQuery(id+"F0.wireOp",EDGE,"E12"),sQuery(id+"F0.wireOp",EDGE,"E13"),sQuery(id+"F0.wireOp",EDGE,"E14"),sQuery(id+"F0.wireOp",EDGE,"E15"),sQuery(id+"F0.wireOp",EDGE,"E17.filletArc"),sQuery(id+"F0.wireOp",EDGE,"E18.filletArc"),sQuery(id+"F0.wireOp",EDGE,"E19.filletArc"),sQuery(id+"F0.wireOp",EDGE,"E20.filletArc"),sQuery(id+"F0.wireOp",EDGE,"E25.0"),sQuery(id+"F0.wireOp",EDGE,"E25.1"),sQuery(id+"F0.wireOp",EDGE,"E25.2"),sQuery(id+"F0.wireOp",EDGE,"E25.3"),sQuery(id+"F0.wireOp",EDGE,"E25.4"),sQuery(id+"F0.wireOp",EDGE,"E25.5"),sQuery(id+"F0.wireOp",EDGE,"E25.6"),sQuery(id+"F0.wireOp",EDGE,"E25.7")])],"isStart":false});
            extrude(context, id + "F17", {"entities" : qUnion([Q0, Q1, Q2]), "endBound" : BoundingType.UP_TO_SURFACE, "depth" : 25 * mm, "endBoundEntityFace" : qUnion([Q3]), "offsetDistance" : 25 * mm});
        }
    });
